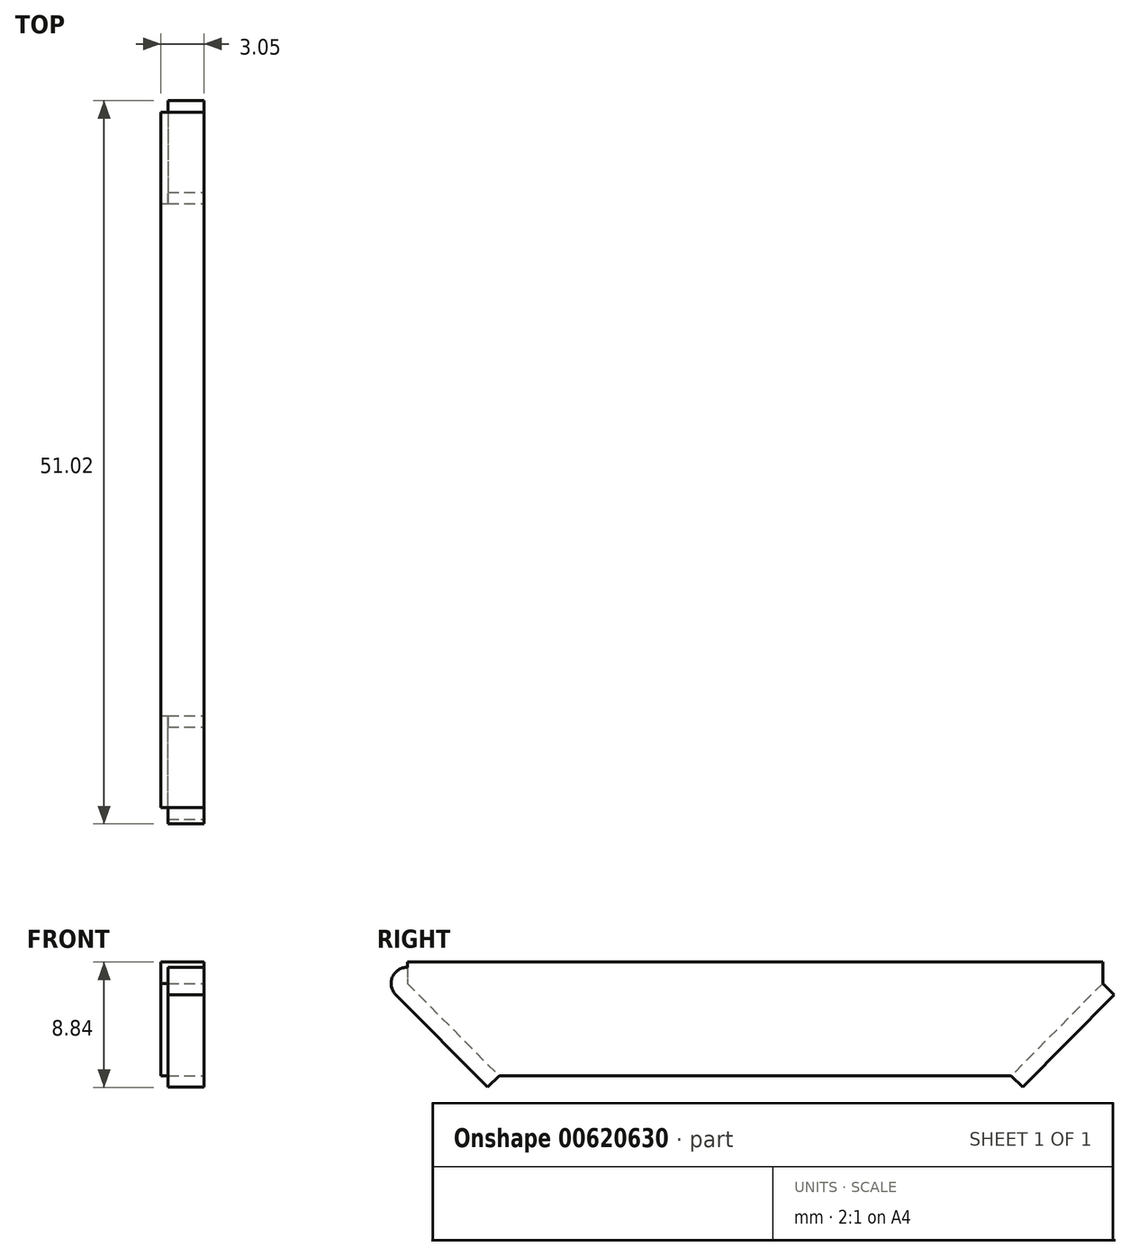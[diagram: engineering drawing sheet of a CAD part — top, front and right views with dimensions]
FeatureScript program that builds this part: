
annotation { "Feature Type Name" : "Feature", "Feature Type Description" : "" }
export const myFeature = defineFeature(function(context is Context, id is Id, definition is map)
    precondition{}
    {
        {
            var Q0;
            Q0=qCreatedBy(makeId("Right.planeOp"),FACE);
            var sketch = newSketch(context, id + "F0", { "sketchPlane" : qUnion([Q0])});
            skLineSegment(sketch, "E0", {"start": v(1.12, -3.75) * mm, "end": v(19.18, -3.75) * mm});
            skLineSegment(sketch, "E1", {"start": v(1.12, -3.75) * mm, "end": v(-16.94, -3.75) * mm});
            skLineSegment(sketch, "E2", {"start": v(1.12, 4.28) * mm, "end": v(-23.42, 4.28) * mm});
            skLineSegment(sketch, "E3", {"start": v(1.12, 4.28) * mm, "end": v(25.64, 4.28) * mm});
            skLineSegment(sketch, "E4", {"start": v(-23.42, 4.28) * mm, "end": v(-23.42, 2.77) * mm});
            skLineSegment(sketch, "E5", {"start": v(-23.42, 2.77) * mm, "end": v(-16.94, -3.75) * mm});
            skLineSegment(sketch, "E6", {"start": v(25.64, 4.28) * mm, "end": v(25.64, 2.77) * mm});
            skLineSegment(sketch, "E7", {"start": v(25.64, 2.77) * mm, "end": v(19.18, -3.75) * mm});
            skLineSegment(sketch, "E8", {"start": v(-16.94, -3.75) * mm, "end": v(19.18, -3.75) * mm});
            skLineSegment(sketch, "E9", {"start": v(-16.94, -3.75) * mm, "end": v(-17.75, -4.56) * mm});
            skLineSegment(sketch, "E10", {"start": v(-23.42, 2.77) * mm, "end": v(-24.23, 1.97) * mm});
            skLineSegment(sketch, "E11", {"start": v(-24.23, 1.97) * mm, "end": v(-17.75, -4.56) * mm});
            skLineSegment(sketch, "E12", {"start": v(19.18, -3.75) * mm, "end": v(20, -4.56) * mm});
            skLineSegment(sketch, "E13", {"start": v(25.64, 2.77) * mm, "end": v(26.46, 1.96) * mm});
            skLineSegment(sketch, "E14", {"start": v(26.46, 1.96) * mm, "end": v(20, -4.56) * mm});
            skArc(sketch, "E15", {"start": v(-23.42, 3.92) * mm, "mid": v(-24.47, 3.21) * mm, "end": v(-24.22, 1.97) * mm});
            skArc(sketch, "E16", {"start": v(25.64, 3.92) * mm, "mid": v(26.7, 3.22) * mm, "end": v(26.45, 1.97) * mm});
            skArc(sketch, "E17", {"start": v(20, -4.56) * mm, "mid": v(19.62, -4.8) * mm, "end": v(19.18, -4.9) * mm});
            skArc(sketch, "E18", {"start": v(-17.75, -4.56) * mm, "mid": v(-17.38, -4.8) * mm, "end": v(-16.94, -4.9) * mm});
            skLineSegment(sketch, "E19", {"start": v(19.18, -4.9) * mm, "end": v(-16.94, -4.9) * mm});
            skSolve(sketch);
        }
        {
            var Q0;
            {var subQ3=sQuery(id+"F0.wireOp",EDGE,"E2");Q0=makeQuery(id+"F0.imprint","IMPRINT",FACE,{"disambiguationData":[TD([[makeQuery(id+"F0.imprint","IMPRINT",EDGE,{"derivedFrom":subQ3}),1.0]])]});}
            extrude(context, id + "F1", {"entities" : qUnion([Q0]), "oppositeDirection" : true, "depth" : 3.05 * mm, "offsetDistance" : 25.4 * mm});
        }
        {
            var Q0;
            {var subQ3=sQuery(id+"F0.wireOp",EDGE,"E16");Q0=makeQuery(id+"F0.imprint","IMPRINT",FACE,{"disambiguationData":[TD([[makeQuery(id+"F0.imprint","IMPRINT",EDGE,{"derivedFrom":subQ3}),-1.0]])]});}
            var Q1;
            {var subQ3=sQuery(id+"F0.wireOp",EDGE,"E7");Q1=makeQuery(id+"F0.imprint","IMPRINT",FACE,{"disambiguationData":[TD([[makeQuery(id+"F0.imprint","IMPRINT",EDGE,{"derivedFrom":subQ3}),1.0]])]});}
            var Q2;
            Q2=makeQuery(id+"F0.imprint","IMPRINT",FACE,{"disambiguationData":[TD([[makeQuery(id+"F0.imprint","IMPRINT",EDGE,{"derivedFrom":sQuery(id+"F0.wireOp",EDGE,"E8")}),-1.0]])]});
            var Q3;
            {var subQ3=sQuery(id+"F0.wireOp",EDGE,"E5");Q3=makeQuery(id+"F0.imprint","IMPRINT",FACE,{"disambiguationData":[TD([[makeQuery(id+"F0.imprint","IMPRINT",EDGE,{"derivedFrom":subQ3}),-1.0]])]});}
            var Q4;
            {var subQ3=sQuery(id+"F0.wireOp",EDGE,"E15");Q4=makeQuery(id+"F0.imprint","IMPRINT",FACE,{"disambiguationData":[TD([[makeQuery(id+"F0.imprint","IMPRINT",EDGE,{"derivedFrom":subQ3}),1.0]])]});}
            extrude(context, id + "F2", {"entities" : qUnion([Q0, Q1, Q2, Q3, Q4]), "operationType" : NewBodyOperationType.ADD, "oppositeDirection" : true, "depth" : 2.54 * mm, "offsetDistance" : 25.4 * mm});
        }
    });
